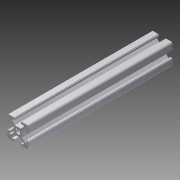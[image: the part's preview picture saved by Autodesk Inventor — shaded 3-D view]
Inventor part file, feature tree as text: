
AUTODESK INVENTOR PART (.ipt)
format: ipt  version: 2015 (Build 190159000, 159)  size: 155,136 bytes
history: native  units: mm
features: extrude x2, mirror x2, sketch x2, fillet x1
ambient origin geometry x8: Origin, YZ Plane, XZ Plane, XY Plane, X Axis, Y Axis, Z Axis, Center Point
bodies: Solid1 (feature_tree)
feature tree (7):
  extrude  "Extrusion1"  Depth=10.0mm
  fillet  "Fillet1"  Radius=10.0mm
  mirror  "Mirror1"
  mirror  "Mirror2"
  extrude  "Extrusion2"  Depth=6.1mm
  sketch  "Sketch1"  dims[d0=45.0deg d1=5.63mm d2=10.0mm]
  sketch  "Sketch2"  dims[d3=3.1mm d5=6.1mm d6=1.5mm d7=2.0mm d8=138.0mm d9=0.0mm d10=1.5mm d11=3.6mm d12=4.45mm d13=10.0mm d14=0.0mm]
